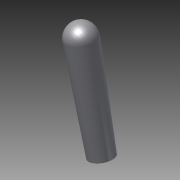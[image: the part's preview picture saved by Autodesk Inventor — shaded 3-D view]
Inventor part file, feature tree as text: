
AUTODESK INVENTOR PART (.ipt)
format: ipt  version: 2014 (Build 180170000, 170)  size: 104,960 bytes
history: native  units: in
note: dims shown in document units (in); Inventor stores cm internally (conversion verified against a paired STEP export)
features: other x14, revolve x1, sketch x1
ambient origin geometry x8: Origin, YZ Plane, XZ Plane, XY Plane, X Axis, Y Axis, Z Axis, Center Point
bodies: Solid1 (feature_tree)
feature tree (16):
  revolve  "Revolution1"  [1 undecoded]
  other  "rot_XY"
  other  "rot_YZ"
  other  "rot_ZX"
  other  "rot_X"
  other  "rot_Y"
  other  "rot_Z"
  other  "rot_Center"
  other  "to_cap_XY"
  other  "to_cap_YZ"
  other  "to_cap_ZX"
  other  "to_cap_X"
  other  "to_cap_Y"
  other  "to_cap_Z"
  other  "to_cap_Center"
  sketch  "Sketch_3"  dims[d0=360.0deg]
note: 1 required parameter value undecoded (feature->parameter linkage not recoverable at this tier; creation-order binding heuristic only, values carry confidence <= 0.55)
